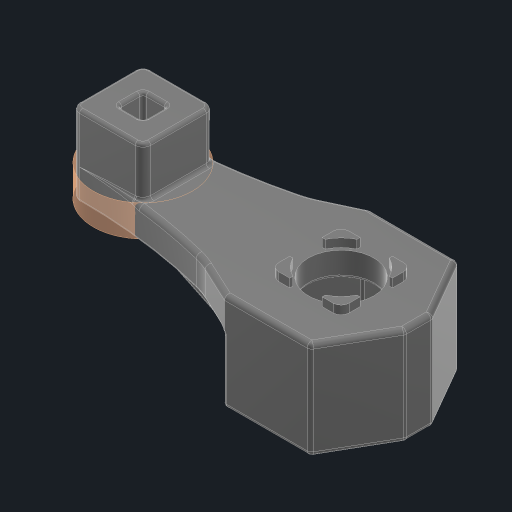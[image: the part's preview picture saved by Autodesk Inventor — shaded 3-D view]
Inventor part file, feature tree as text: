
AUTODESK INVENTOR PART (.ipt)
format: ipt  version: 2023 (Build 270158030, 158C)  size: 462,848 bytes
history: native  units: in
note: dims shown in document units (in); Inventor stores cm internally (conversion verified against a paired STEP export)
features: extrude x2, sketch x2, projected_geometry x1, other x1, fillet x1
ambient origin geometry x8: Origin, YZ Plane, XZ Plane, XY Plane, X Axis, Y Axis, Z Axis, Center Point
bodies: Solid1 (feature_tree)
feature tree (7):
  extrude  "Extrusion1"  Depth=0.3937in TaperAngle=0.0deg
  sketch  "Sketch1"  dims[d0=0.25in d1=0.3937in d2=0.0in d3=0.0394in d4=0.0in]
  projected_geometry  "Projected Loop1"
  other  "Srf1"
  sketch  "Sketch2"
  fillet  "Fillet16"  Radius=0.0394in
  extrude  "ExtrusionSrf1"  [1 undecoded]
note: 1 required parameter value undecoded (feature->parameter linkage not recoverable at this tier; creation-order binding heuristic only, values carry confidence <= 0.55)
